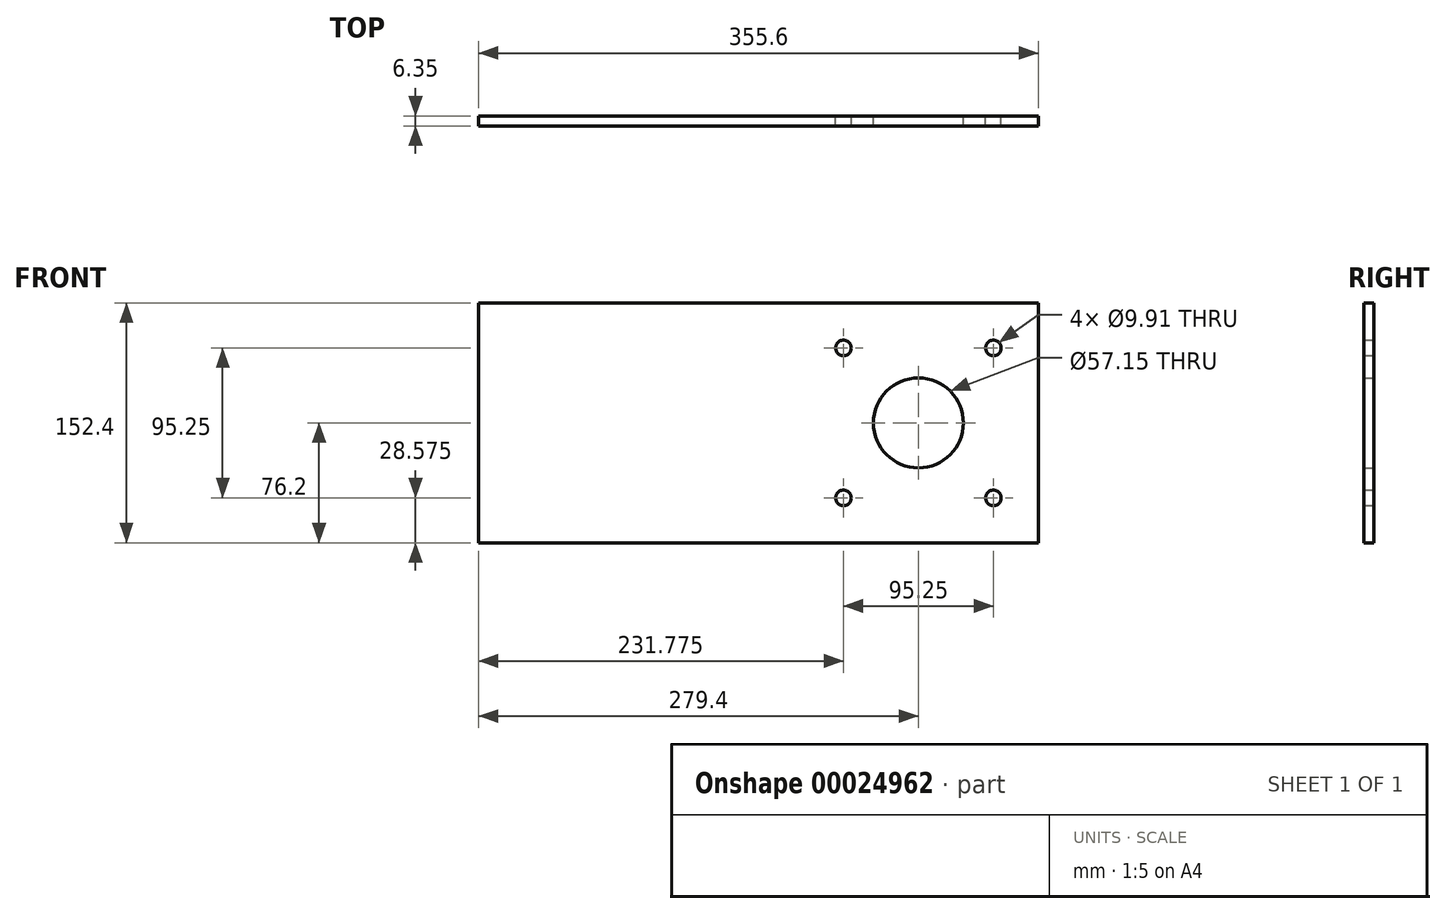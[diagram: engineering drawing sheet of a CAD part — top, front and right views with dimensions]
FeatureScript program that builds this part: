
annotation { "Feature Type Name" : "Feature", "Feature Type Description" : "" }
export const myFeature = defineFeature(function(context is Context, id is Id, definition is map)
    precondition{}
    {
        {
            var Q0;
            Q0=qCreatedBy(makeId("Front.planeOp"),FACE);
            var sketch = newSketch(context, id + "F0", { "sketchPlane" : qUnion([Q0])});
            skLineSegment(sketch, "E0.bottom", {"start": v(0, 0) * mm, "end": v(355.6, 0) * mm});
            skLineSegment(sketch, "E0.top", {"start": v(0, 152.4) * mm, "end": v(355.6, 152.4) * mm});
            skLineSegment(sketch, "E0.left", {"start": v(0, 0) * mm, "end": v(0, 152.4) * mm});
            skLineSegment(sketch, "E0.right", {"start": v(355.6, 0) * mm, "end": v(355.6, 152.4) * mm});
            skCircle(sketch, "E1", {"center": v(279.4, 76.2) * mm, "radius": 28.58 * mm});
            skLineSegment(sketch, "E2", {"start": v(279.4, 76.2) * mm, "end": v(355.6, 76.2) * mm, "construction": true});
            skLineSegment(sketch, "E3", {"start": v(279.4, 76.2) * mm, "end": v(231.78, 123.82) * mm, "construction": true});
            skCircle(sketch, "E4", {"center": v(231.78, 123.82) * mm, "radius": 4.95 * mm});
            skCircle(sketch, "E5.1.0", {"center": v(231.78, 28.57) * mm, "radius": 4.95 * mm});
            skCircle(sketch, "E5.2.0", {"center": v(327.03, 28.58) * mm, "radius": 4.95 * mm});
            skCircle(sketch, "E5.3.0", {"center": v(327.02, 123.82) * mm, "radius": 4.95 * mm});
            skSolve(sketch);
        }
        {
            var Q0;
            Q0 = qSketchRegion(id + "F0", true);
            extrude(context, id + "F1", {"entities" : qUnion([Q0]), "depth" : 6.35 * mm});
        }
    });
